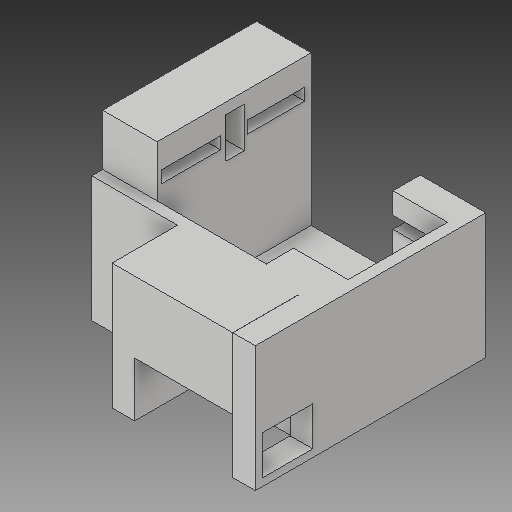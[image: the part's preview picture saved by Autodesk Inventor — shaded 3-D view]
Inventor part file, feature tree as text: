
AUTODESK INVENTOR PART (.ipt)
format: ipt  version: 2018 (Build 220112000, 112)  size: 232,960 bytes
history: native  units: in
note: dims shown in document units (in); Inventor stores cm internally (conversion verified against a paired STEP export)
features: extrude x10, sketch x10
ambient origin geometry x8: Origin, YZ Plane, XZ Plane, XY Plane, X Axis, Y Axis, Z Axis, Center Point
bodies: Solid1 (feature_tree)
feature tree (20):
  extrude  "Extrusion1"  Depth=0.9in
  extrude  "Extrusion2"  Depth=0.1in
  extrude  "Extrusion3"  Depth=0.1in
  sketch  "Sketch4"  dims[d9=1.15in d11=0.25in]
  extrude  "Extrusion7"  Depth=0.25in
  extrude  "Extrusion8"  Depth=0.1in TaperAngle=0.0deg
  extrude  "Extrusion9"  Depth=1.4115in
  extrude  "Extrusion11"  Depth=1.0in
  extrude  "Extrusion12"  Depth=0.175in
  extrude  "Extrusion13"  Depth=0.1in TaperAngle=0.0deg
  extrude  "Extrusion14"  Depth=0.9in
  sketch  "Sketch1"  dims[d0=0.9in d1=0.9in]
  sketch  "Sketch2"  dims[d4=0.2in d5=0.1in]
  sketch  "Sketch3"  dims[d6=0.2in d7=0.1in]
  sketch  "Sketch6"  dims[d12=0.5in d13=0.0in d14=0.1in d15=0.0in]
  sketch  "Sketch7"  dims[d16=1.15in d17=1.4115in]
  sketch  "Sketch8"  dims[d18=1.0in d19=0.0in d21=0.875in]
  sketch  "Sketch9"  dims[d23=0.0875in d24=0.175in]
  sketch  "Sketch10"  dims[d31=0.5in d32=0.0in d33=0.1in d34=0.0in]
  sketch  "Sketch11"  dims[d35=0.1in d36=0.0in d37=0.9in d39=0.207in d42=1.15in d43=0.0in d44=0.5in d45=0.6125in d46=0.0in d47=0.6125in d48=0.0in d49=0.6125in d50=0.0in]
